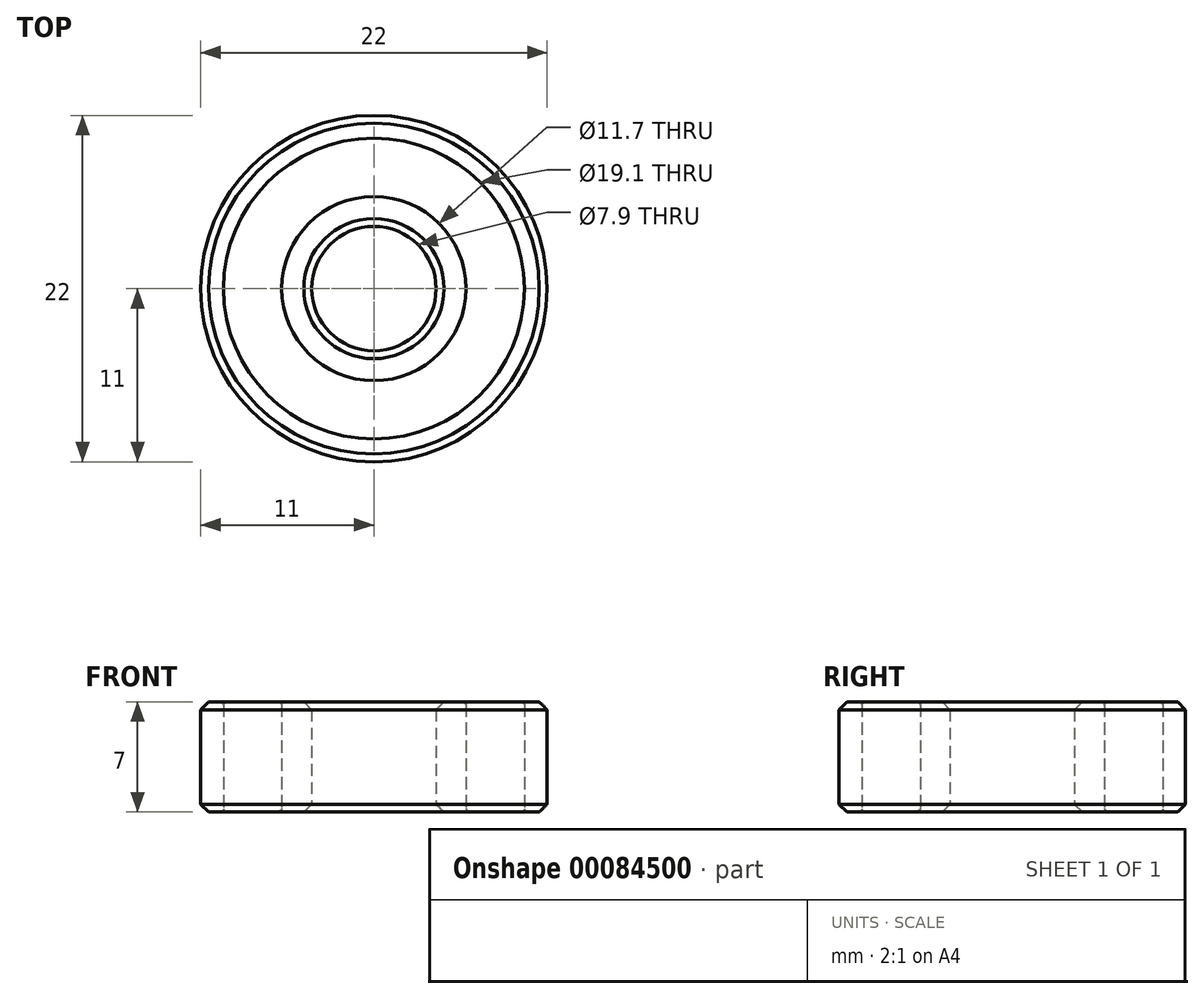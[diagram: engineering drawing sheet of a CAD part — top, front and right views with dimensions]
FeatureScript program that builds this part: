
annotation { "Feature Type Name" : "Feature", "Feature Type Description" : "" }
export const myFeature = defineFeature(function(context is Context, id is Id, definition is map)
    precondition{}
    {
        {
            var Q0;
            Q0=qCreatedBy(makeId("Top.planeOp"),FACE);
            var sketch = newSketch(context, id + "F0", { "sketchPlane" : qUnion([Q0])});
            skCircle(sketch, "E0", {"center": v(0, 0) * mm, "radius": 11 * mm});
            skCircle(sketch, "E1", {"center": v(0, 0) * mm, "radius": 9.55 * mm});
            skPoint(sketch, "E2", {"position": v(9.55, 0) * mm});
            skPoint(sketch, "E3", {"position": v(11, 0) * mm});
            skCircle(sketch, "E4", {"center": v(0, 0) * mm, "radius": 5.85 * mm});
            skPoint(sketch, "E5", {"position": v(5.85, 0) * mm});
            skCircle(sketch, "E6", {"center": v(0, 0) * mm, "radius": 3.95 * mm});
            skPoint(sketch, "E7", {"position": v(3.95, 0) * mm});
            skPoint(sketch, "E8", {"position": v(-3.95, 0) * mm});
            skSolve(sketch);
        }
        {
            var Q0;
            Q0=makeQuery(id+"F0.imprint","IMPRINT",FACE,{"disambiguationData":[TD([[makeQuery(id+"F0.imprint","IMPRINT",EDGE,{"derivedFrom":sQuery(id+"F0.wireOp",EDGE,"E0")}),1.0]])]});
            var Q1;
            Q1=makeQuery(id+"F0.imprint","IMPRINT",FACE,{"disambiguationData":[TD([[makeQuery(id+"F0.imprint","IMPRINT",EDGE,{"derivedFrom":sQuery(id+"F0.wireOp",EDGE,"E4")}),1.0]])]});
            extrude(context, id + "F1", {"entities" : qUnion([Q0, Q1]), "endBound" : BoundingType.SYMMETRIC, "depth" : 7 * mm});
        }
        {
            var Q0;
            Q0=makeQuery(id+"F0.imprint","IMPRINT",FACE,{"disambiguationData":[TD([[makeQuery(id+"F0.imprint","IMPRINT",EDGE,{"derivedFrom":sQuery(id+"F0.wireOp",EDGE,"E1")}),1.0]])]});
            extrude(context, id + "F2", {"entities" : qUnion([Q0]), "endBound" : BoundingType.SYMMETRIC, "depth" : 6.9 * mm});
        }
        {
            var Q0;
            Q0=makeQuery(id+"F1.opExtrude","CAP_EDGE",EDGE,{"disambiguationData":[OSD([sQuery(id+"F0.wireOp",EDGE,"E0")])],"isStart":false});
            var Q1;
            Q1=makeQuery(id+"F1.opExtrude","CAP_EDGE",EDGE,{"disambiguationData":[OSD([sQuery(id+"F0.wireOp",EDGE,"E0")])],"isStart":true});
            var Q2;
            Q2=makeQuery(id+"F1.opExtrude","CAP_EDGE",EDGE,{"disambiguationData":[OSD([sQuery(id+"F0.wireOp",EDGE,"E6")])],"isStart":false});
            var Q3;
            Q3=makeQuery(id+"F1.opExtrude","CAP_EDGE",EDGE,{"disambiguationData":[OSD([sQuery(id+"F0.wireOp",EDGE,"E6")])],"isStart":true});
            chamfer(context, id + "F3", {"entities" : qUnion([Q0, Q1, Q2, Q3]), "width" : .5 * mm, "tangentPropagation" : true});
        }
        {
            var Q0;
            Q0=makeQuery(id+"F1.opExtrude","CAP_EDGE",EDGE,{"disambiguationData":[OSD([sQuery(id+"F0.wireOp",EDGE,"E4")])],"isStart":false});
            var Q1;
            Q1=makeQuery(id+"F1.opExtrude","CAP_EDGE",EDGE,{"disambiguationData":[OSD([sQuery(id+"F0.wireOp",EDGE,"E1")])],"isStart":false});
            var Q2;
            Q2=makeQuery(id+"F2.opExtrude","CAP_EDGE",EDGE,{"disambiguationData":[OSD([sQuery(id+"F0.wireOp",EDGE,"E4")])],"isStart":true});
            var Q3;
            Q3=makeQuery(id+"F1.opExtrude","CAP_EDGE",EDGE,{"disambiguationData":[OSD([sQuery(id+"F0.wireOp",EDGE,"E1")])],"isStart":true});
            fillet(context, id + "F4", {"entities" : qUnion([Q0, Q1, Q2, Q3]), "radius" : .2 * mm, "tangentPropagation" : true, "allowEdgeOverflow" : false});
        }
        {
            var Q0;
            Q0=makeQuery(id+"F2.opExtrude","CAP_EDGE",EDGE,{"disambiguationData":[OSD([sQuery(id+"F0.wireOp",EDGE,"E4")])],"isStart":false});
            var Q1;
            Q1=makeQuery(id+"F2.opExtrude","CAP_EDGE",EDGE,{"disambiguationData":[OSD([sQuery(id+"F0.wireOp",EDGE,"E1")])],"isStart":false});
            var Q2;
            Q2=makeQuery(id+"F2.opExtrude","CAP_EDGE",EDGE,{"disambiguationData":[OSD([sQuery(id+"F0.wireOp",EDGE,"E1")])],"isStart":true});
            var Q3;
            {var subQ0=sQuery(id+"F0.wireOp",EDGE,"E4");Q3=makeQuery(id+"F4.opFillet","BLEND_FACE",FACE,{"disambiguationData":[OSD([subQ0]),TDD([makeQuery(id+"F2.opExtrude","CAP_EDGE",EDGE,{"disambiguationData":[OSD([subQ0])],"isStart":true})])]});}
            fillet(context, id + "F5", {"entities" : qUnion([Q0, Q1, Q2, Q3]), "radius" : .1 * mm, "tangentPropagation" : true, "allowEdgeOverflow" : false});
        }
    });
